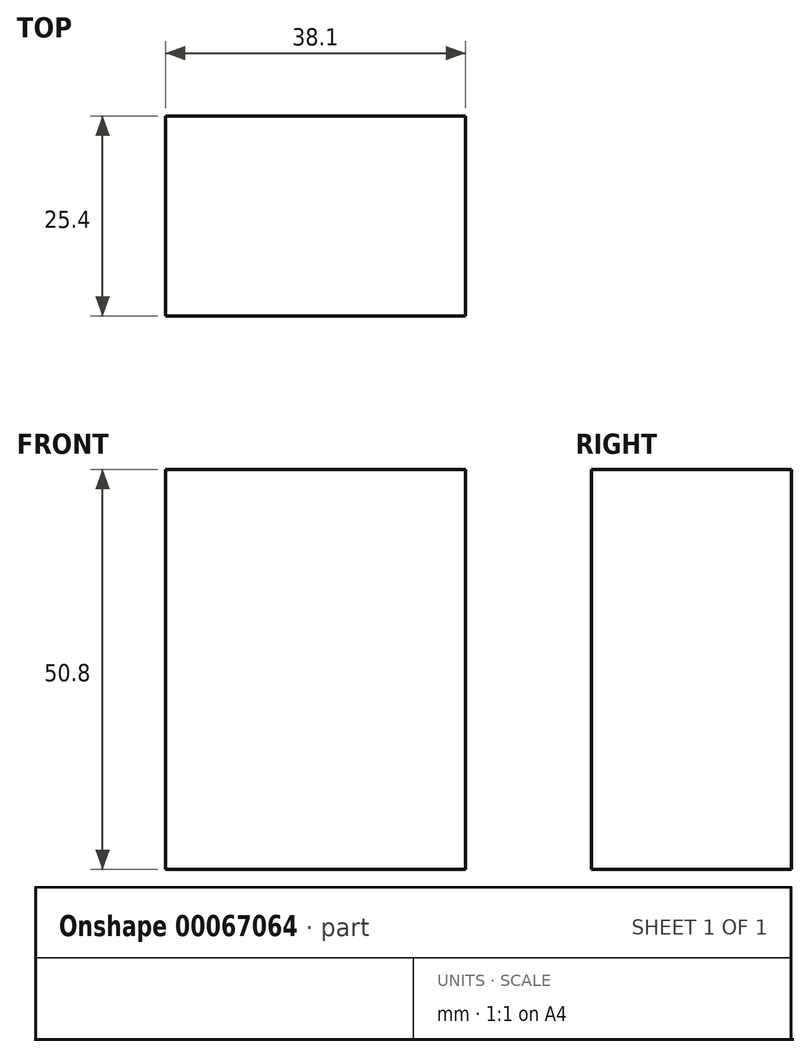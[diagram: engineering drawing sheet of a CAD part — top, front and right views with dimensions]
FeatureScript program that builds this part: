
annotation { "Feature Type Name" : "Feature", "Feature Type Description" : "" }
export const myFeature = defineFeature(function(context is Context, id is Id, definition is map)
    precondition{}
    {
        {
            var Q0;
            Q0=qCreatedBy(makeId("Front.planeOp"),FACE);
            var sketch = newSketch(context, id + "F0", { "sketchPlane" : qUnion([Q0])});
            skLineSegment(sketch, "E0", {"start": v(0, 0) * mm, "end": v(0, 50.8) * mm});
            skLineSegment(sketch, "E1", {"start": v(0, 50.8) * mm, "end": v(38.1, 50.8) * mm});
            skLineSegment(sketch, "E2", {"start": v(38.1, 50.8) * mm, "end": v(38.1, 0) * mm});
            skLineSegment(sketch, "E3", {"start": v(38.1, 0) * mm, "end": v(0, 0) * mm});
            skSolve(sketch);
        }
        {
            var Q0;
            Q0 = qSketchRegion(id + "F0", true);
            extrude(context, id + "F1", {"entities" : qUnion([Q0]), "depth" : 25.4 * mm});
        }
    });
